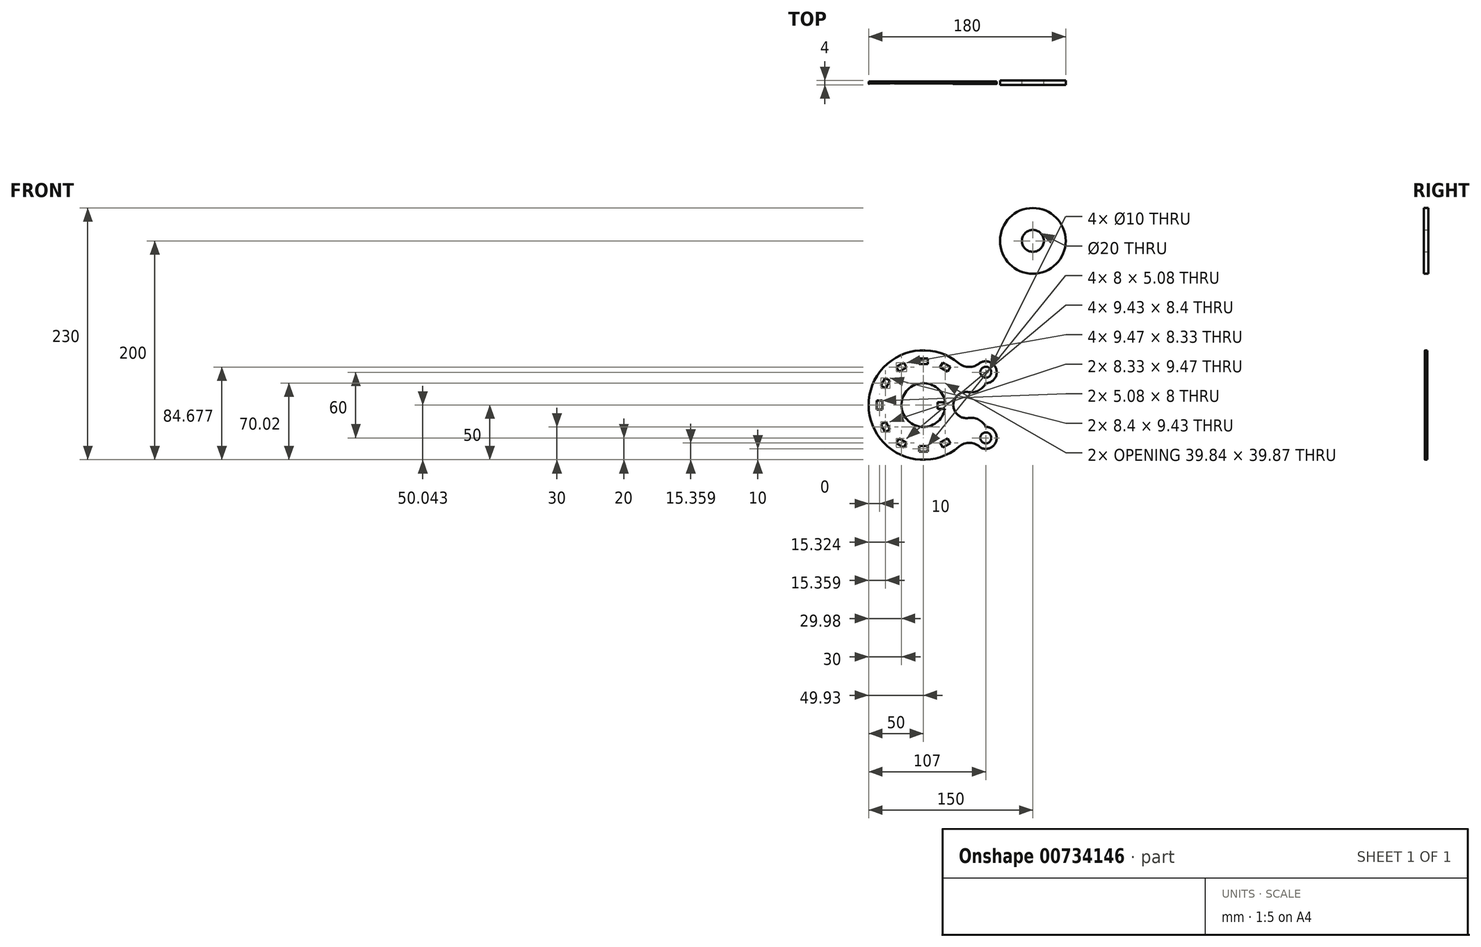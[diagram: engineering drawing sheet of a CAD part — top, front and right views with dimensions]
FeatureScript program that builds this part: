
annotation { "Feature Type Name" : "Feature", "Feature Type Description" : "" }
export const myFeature = defineFeature(function(context is Context, id is Id, definition is map)
    precondition{}
    {
        {
            var Q0;
            Q0=qCreatedBy(makeId("Front.planeOp"),FACE);
            var sketch = newSketch(context, id + "F0", { "sketchPlane" : qUnion([Q0])});
            skLineSegment(sketch, "E0", {"start": v(12.85, 2.43) * mm, "end": v(12.85, -3.57) * mm});
            skLineSegment(sketch, "E1", {"start": v(12.85, -3.57) * mm, "end": v(19.85, -3.57) * mm});
            skLineSegment(sketch, "E2", {"start": v(12.85, 2.43) * mm, "end": v(19.85, 2.43) * mm});
            skArc(sketch, "E3", {"start": v(19.85, 2.43) * mm, "mid": v(-20, 0.57) * mm, "end": v(19.68, -3.57) * mm});
            skArc(sketch, "E4.0", {"start": v(32.12, 38.32) * mm, "mid": v(-50, -0.12) * mm, "end": v(32.3, -38.16) * mm});
            skArc(sketch, "E5", {"start": v(51.4, 38.28) * mm, "mid": v(66.56, 32.93) * mm, "end": v(57, 20) * mm});
            skArc(sketch, "E6", {"start": v(57, -20) * mm, "mid": v(66.74, -32.27) * mm, "end": v(52.57, -38.97) * mm});
            skCircle(sketch, "E7", {"center": v(57, -30) * mm, "radius": 5 * mm});
            skCircle(sketch, "E8", {"center": v(57, 30) * mm, "radius": 5 * mm});
            skLineSegment(sketch, "E9", {"start": v(24.73, -34.84) * mm, "end": v(17.8, -38.84) * mm});
            skLineSegment(sketch, "E10", {"start": v(15.27, -34.44) * mm, "end": v(17.8, -38.84) * mm});
            skLineSegment(sketch, "E11", {"start": v(24.73, -34.84) * mm, "end": v(22.23, -30.51) * mm});
            skLineSegment(sketch, "E12", {"start": v(22.23, -30.51) * mm, "end": v(15.27, -34.44) * mm});
            skLineSegment(sketch, "E13.1.0", {"start": v(4, -42.54) * mm, "end": v(-4, -42.54) * mm});
            skLineSegment(sketch, "E13.1.1", {"start": v(4, -37.54) * mm, "end": v(-4, -37.46) * mm});
            skLineSegment(sketch, "E13.1.2", {"start": v(4, -42.54) * mm, "end": v(4, -37.54) * mm});
            skLineSegment(sketch, "E13.1.3", {"start": v(-4, -37.46) * mm, "end": v(-4, -42.54) * mm});
            skLineSegment(sketch, "E13.2.0", {"start": v(-17.8, -38.84) * mm, "end": v(-24.73, -34.84) * mm});
            skLineSegment(sketch, "E13.2.1", {"start": v(-15.3, -34.51) * mm, "end": v(-22.2, -30.44) * mm});
            skLineSegment(sketch, "E13.2.2", {"start": v(-17.8, -38.84) * mm, "end": v(-15.3, -34.51) * mm});
            skLineSegment(sketch, "E13.2.3", {"start": v(-22.2, -30.44) * mm, "end": v(-24.73, -34.84) * mm});
            skLineSegment(sketch, "E13.3.0", {"start": v(-34.84, -24.73) * mm, "end": v(-38.84, -17.8) * mm});
            skLineSegment(sketch, "E13.3.1", {"start": v(-30.51, -22.23) * mm, "end": v(-34.44, -15.27) * mm});
            skLineSegment(sketch, "E13.3.2", {"start": v(-34.84, -24.73) * mm, "end": v(-30.51, -22.23) * mm});
            skLineSegment(sketch, "E13.3.3", {"start": v(-34.44, -15.27) * mm, "end": v(-38.84, -17.8) * mm});
            skLineSegment(sketch, "E13.4.0", {"start": v(-42.54, -4) * mm, "end": v(-42.54, 4) * mm});
            skLineSegment(sketch, "E13.4.1", {"start": v(-37.54, -4) * mm, "end": v(-37.46, 4) * mm});
            skLineSegment(sketch, "E13.4.2", {"start": v(-42.54, -4) * mm, "end": v(-37.54, -4) * mm});
            skLineSegment(sketch, "E13.4.3", {"start": v(-37.46, 4) * mm, "end": v(-42.54, 4) * mm});
            skLineSegment(sketch, "E13.5.0", {"start": v(-38.84, 17.8) * mm, "end": v(-34.84, 24.73) * mm});
            skLineSegment(sketch, "E13.5.1", {"start": v(-34.51, 15.3) * mm, "end": v(-30.44, 22.2) * mm});
            skLineSegment(sketch, "E13.5.2", {"start": v(-38.84, 17.8) * mm, "end": v(-34.51, 15.3) * mm});
            skLineSegment(sketch, "E13.5.3", {"start": v(-30.44, 22.2) * mm, "end": v(-34.84, 24.73) * mm});
            skLineSegment(sketch, "E13.6.0", {"start": v(-24.73, 34.84) * mm, "end": v(-17.8, 38.84) * mm});
            skLineSegment(sketch, "E13.6.1", {"start": v(-22.23, 30.51) * mm, "end": v(-15.27, 34.44) * mm});
            skLineSegment(sketch, "E13.6.2", {"start": v(-24.73, 34.84) * mm, "end": v(-22.23, 30.51) * mm});
            skLineSegment(sketch, "E13.6.3", {"start": v(-15.27, 34.44) * mm, "end": v(-17.8, 38.84) * mm});
            skLineSegment(sketch, "E13.7.0", {"start": v(-4, 42.54) * mm, "end": v(4, 42.54) * mm});
            skLineSegment(sketch, "E13.7.1", {"start": v(-4, 37.54) * mm, "end": v(4, 37.46) * mm});
            skLineSegment(sketch, "E13.7.2", {"start": v(-4, 42.54) * mm, "end": v(-4, 37.54) * mm});
            skLineSegment(sketch, "E13.7.3", {"start": v(4, 37.46) * mm, "end": v(4, 42.54) * mm});
            skLineSegment(sketch, "E13.8.0", {"start": v(17.8, 38.84) * mm, "end": v(24.73, 34.84) * mm});
            skLineSegment(sketch, "E13.8.1", {"start": v(15.3, 34.51) * mm, "end": v(22.2, 30.44) * mm});
            skLineSegment(sketch, "E13.8.2", {"start": v(17.8, 38.84) * mm, "end": v(15.3, 34.51) * mm});
            skLineSegment(sketch, "E13.8.3", {"start": v(22.2, 30.44) * mm, "end": v(24.73, 34.84) * mm});
            skArc(sketch, "E14", {"start": v(52.57, -38.97) * mm, "mid": v(42.6, -34.62) * mm, "end": v(32.3, -38.16) * mm});
            skArc(sketch, "E15", {"start": v(41.2, 11.85) * mm, "mid": v(50.44, 13.33) * mm, "end": v(57, 20) * mm});
            skArc(sketch, "E16", {"start": v(57, -20) * mm, "mid": v(50.44, -13.33) * mm, "end": v(41.2, -11.85) * mm});
            skArc(sketch, "E17", {"start": v(63.49, -37.6) * mm, "mid": v(123.1, 50.25) * mm, "end": v(129.34, 156.25) * mm});
            skArc(sketch, "E18", {"start": v(-23.83, 43.95) * mm, "mid": v(34.95, 92.3) * mm, "end": v(71.41, 159.1) * mm});
            skCircle(sketch, "E19", {"center": v(100, 150) * mm, "radius": 30 * mm});
            skCircle(sketch, "E20", {"center": v(100, 150) * mm, "radius": 10 * mm});
            skArc(sketch, "E21", {"start": v(41.2, -11.85) * mm, "mid": v(27.32, 0) * mm, "end": v(41.2, 11.85) * mm});
            skArc(sketch, "E22", {"start": v(32.12, 38.32) * mm, "mid": v(41.75, 34.8) * mm, "end": v(51.4, 38.28) * mm});
            skSolve(sketch);
        }
        {
            var Q0;
            Q0=makeQuery(id+"F0.imprint","IMPRINT",FACE,{"disambiguationData":[TD([[makeQuery(id+"F0.imprint","IMPRINT",EDGE,{"derivedFrom":sQuery(id+"F0.wireOp",EDGE,"E20")}),-1.0]])]});
            extrude(context, id + "F1", {"entities" : qUnion([Q0]), "endBound" : BoundingType.SYMMETRIC, "depth" : 4 * mm, "offsetDistance" : 25 * mm});
        }
        {
            var Q0;
            {var subQ7=sQuery(id+"F0.wireOp",EDGE,"E0");Q0=makeQuery(id+"F0.imprint","IMPRINT",FACE,{"disambiguationData":[TD([[makeQuery(id+"F0.imprint","IMPRINT",EDGE,{"derivedFrom":subQ7}),1.0]])]});}
            extrude(context, id + "F2", {"entities" : qUnion([Q0]), "endBound" : BoundingType.SYMMETRIC, "depth" : 2.3 * mm, "offsetDistance" : 25 * mm});
        }
        {
            var Q0;
            Q0=makeQuery(id+"F0.imprint","IMPRINT",FACE,{"disambiguationData":[TD([[makeQuery(id+"F0.imprint","IMPRINT",EDGE,{"derivedFrom":sQuery(id+"F0.wireOp",EDGE,"E5")}),1.0]])]});
            extrude(context, id + "F3", {"entities" : qUnion([Q0]), "endBound" : BoundingType.SYMMETRIC, "depth" : 1.2 * mm, "offsetDistance" : 25 * mm});
        }
        {
            var Q0;
            Q0=makeQuery(id+"F2.opExtrude","CAP_EDGE",EDGE,{"disambiguationData":[OSD([sQuery(id+"F0.wireOp",EDGE,"E22")])],"isStart":false});
            var Q1;
            Q1=makeQuery(id+"F2.opExtrude","CAP_EDGE",EDGE,{"disambiguationData":[OSD([sQuery(id+"F0.wireOp",EDGE,"E5")])],"isStart":false});
            var Q2;
            Q2=makeQuery(id+"F2.opExtrude","CAP_EDGE",EDGE,{"disambiguationData":[OSD([sQuery(id+"F0.wireOp",EDGE,"E15")])],"isStart":false});
            var Q3;
            Q3=makeQuery(id+"F2.opExtrude","CAP_EDGE",EDGE,{"disambiguationData":[OSD([sQuery(id+"F0.wireOp",EDGE,"E21")])],"isStart":false});
            var Q4;
            Q4=makeQuery(id+"F2.opExtrude","CAP_EDGE",EDGE,{"disambiguationData":[OSD([sQuery(id+"F0.wireOp",EDGE,"E16")])],"isStart":false});
            var Q5;
            Q5=makeQuery(id+"F2.opExtrude","CAP_EDGE",EDGE,{"disambiguationData":[OSD([sQuery(id+"F0.wireOp",EDGE,"E6")])],"isStart":false});
            var Q6;
            Q6=makeQuery(id+"F2.opExtrude","CAP_EDGE",EDGE,{"disambiguationData":[OSD([sQuery(id+"F0.wireOp",EDGE,"E14")])],"isStart":false});
            var Q7;
            Q7=makeQuery(id+"F2.opExtrude","CAP_EDGE",EDGE,{"disambiguationData":[OSD([sQuery(id+"F0.wireOp",EDGE,"E4.0")])],"isStart":false});
            fillet(context, id + "F4", {"entities" : qUnion([Q0, Q1, Q2, Q3, Q4, Q5, Q6, Q7]), "radius" : .25 * mm, "tangentPropagation" : true, "allowEdgeOverflow" : false});
        }
    });
